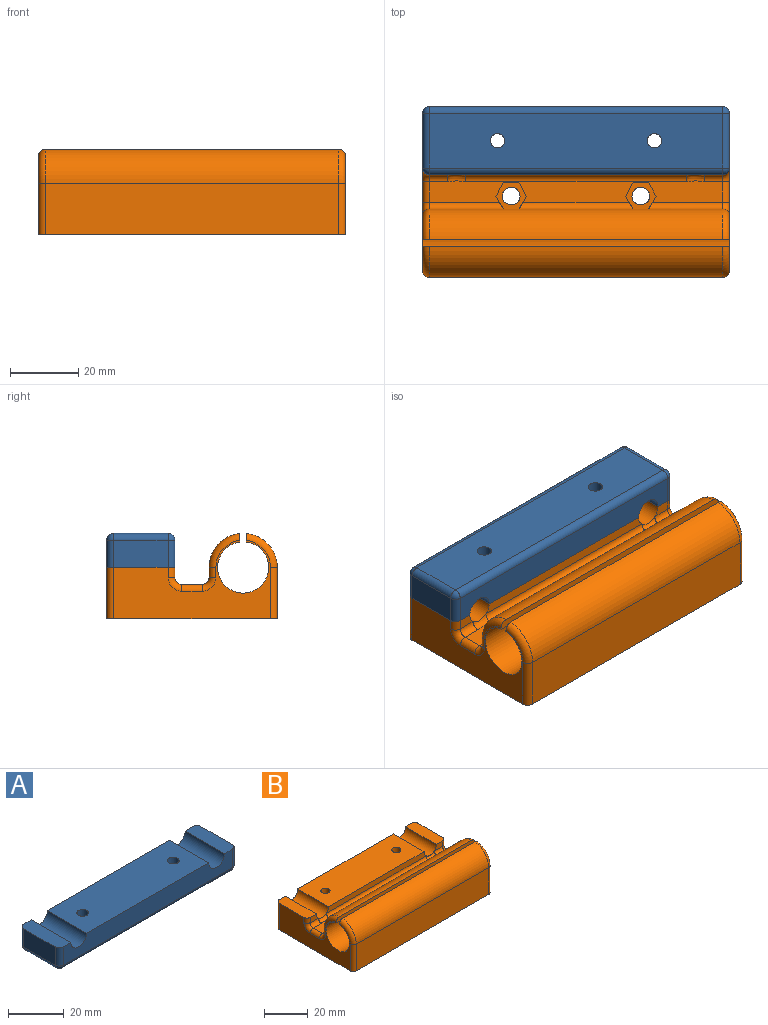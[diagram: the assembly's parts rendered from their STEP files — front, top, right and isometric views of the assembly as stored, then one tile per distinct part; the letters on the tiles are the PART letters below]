
ASSEMBLY  parts=2 mates=1
PART A: 24 faces, bbox 90x20x10 mm
  f0: plane 62x20mm, normal (0,0,1), area 1212.3mm2, adj f2,f4,f8,f9,f10,f11
  f1: plane 20x6mm, normal (0,0,1), area 118.3mm2, adj f2,f3,f4,f10,f14,f23
  f2: plane 86x8mm, normal (0,-1,0), area 637.7mm2, adj f0,f1,f6,f10,f11,f17,f21,f23
  f3: plane 16x8mm, normal (1,0,0), area 128mm2, adj f1,f14,f20,f23
  f4: plane 86x8mm, normal (0,1,0), area 637.7mm2, adj f0,f1,f6,f10,f11,f12,f14,f15
  f5: plane 16x8mm, normal (-1,0,0), area 128mm2, adj f6,f12,f16,f17
  f6: plane 20x6mm, normal (0,0,1), area 118.3mm2, adj f2,f4,f5,f11,f12,f17
  f7: plane 86x16mm, normal (0,0,-1), area 1348.3mm2, adj f8,f9,f15,f16,f20,f21
  f8: cylinder r=2.1mm len=10mm, axis (0,0,1), area 131.9mm2, adj f0,f7
  f9: cylinder r=2.1mm len=10mm, axis (0,0,1), area 131.9mm2, adj f0,f7
  f10: cylinder r=4mm len=20mm, axis (0,-1,0), area 251.3mm2, adj f0,f1,f2,f4
  f11: cylinder r=4mm len=20mm, axis (0,-1,0), area 251.3mm2, adj f0,f2,f4,f6
  f12: cylinder r=2mm len=8mm, axis (0,0,1), area 25.1mm2, adj f4,f5,f6,f13
  f13: sphere r=2mm, area 6.3mm2, adj f12,f15,f16
  f14: cylinder r=2mm len=8mm, axis (0,0,-1), area 25.1mm2, adj f1,f3,f4,f18
  f15: cylinder r=2mm len=86mm, axis (-1,0,0), area 270.2mm2, adj f4,f7,f13,f18
  f16: cylinder r=2mm len=16mm, axis (0,-1,0), area 50.3mm2, adj f5,f7,f13,f19
  f17: cylinder r=2mm len=8mm, axis (0,0,-1), area 25.1mm2, adj f2,f5,f6,f19
  f18: sphere r=2mm, area 6.3mm2, adj f14,f15,f20
  f19: sphere r=2mm, area 6.3mm2, adj f16,f17,f21
  f20: cylinder r=2mm len=16mm, axis (0,1,0), area 50.3mm2, adj f3,f7,f18,f22
  f21: cylinder r=2mm len=86mm, axis (1,0,0), area 270.2mm2, adj f2,f7,f19,f22
  f22: sphere r=2mm, area 6.3mm2, adj f20,f21,f23
  f23: cylinder r=2mm len=8mm, axis (0,0,1), area 25.1mm2, adj f1,f2,f3,f22
PART B: 271 faces, bbox 90.5x51.3x26.3 mm
  f0: plane 90x50mm, normal (0,0,-1), area 4154.4mm2, adj f7,f9,f10,f11,f13,f15,f36,f37
  f1: plane 5.35x3mm, normal (0,-1,0), area 13.2mm2, adj f6,f34,f55,f57
  f2: plane 64.71x3mm, normal (0,-1,0), area 188.5mm2, adj f5,f34,f35,f62
  f3: cylinder r=2.1mm len=11.5mm, axis (0,0,1), area 151.7mm2, adj f5,f49
  f4: cylinder r=2.1mm len=11.5mm, axis (0,0,1), area 151.7mm2, adj f5,f42
  f5: plane 62x20mm, normal (0,0,1), area 1212.3mm2, adj f2,f3,f4,f7,f34,f35
  f6: plane 20x6mm, normal (0,0,1), area 118.3mm2, adj f1,f7,f11,f34,f55,f75
  f7: plane 86x15mm, normal (0,1,0), area 1239.7mm2, adj f0,f5,f6,f33,f34,f35,f74,f75
  f8: plane 86x6.27mm, normal (0,0,1), area 436.2mm2, adj f20,f21,f22,f23,f24,f26,f27,f28
  f9: cylinder r=2.6mm len=6mm, axis (0,0,-1), area 98mm2, adj f0,f31
  f10: cylinder r=2.6mm len=6mm, axis (0,0,-1), area 98mm2, adj f0,f25
  f11: plane 46x22.94mm, normal (-1,0,0), area 521.7mm2, adj f0,f6,f17,f18,f19,f50,f52,f53
  f12: cylinder r=10mm len=86mm, axis (-1,0,0), area 1267.5mm2, adj f14,f18,f50,f58
  f13: plane 46x22.94mm, normal (1,0,0), area 521.7mm2, adj f0,f17,f18,f19,f33,f58,f60,f63
  f14: plane 86x9mm, normal (0,1,0), area 313.3mm2, adj f12,f21,f22,f25,f26,f30,f31,f51
  f15: plane 86x15mm, normal (0,-1,0), area 1290mm2, adj f0,f16,f69,f72
  f16: cylinder r=10mm len=86mm, axis (-1,0,0), area 1267.5mm2, adj f15,f19,f70,f73
  f17: cylinder r=7.5mm len=90mm, axis (-1,0,0), area 4066.5mm2, adj f11,f13,f18,f19
  f18: plane 90.12x2.63mm, normal (0,-1,0), area 224.7mm2, adj f11,f12,f13,f17,f50,f58
  f19: plane 90.12x2.63mm, normal (0,1,0), area 224.7mm2, adj f11,f13,f16,f17,f70,f73
  f20: plane 4x3.9mm, normal (0.87,-0.5,0), area 18mm2, adj f8,f21,f24,f25
  f21: plane 6.49x4.29mm, normal (0.87,0.5,0), area 18.5mm2, adj f8,f14,f20,f25,f71
  f22: plane 6.49x4.29mm, normal (-0.87,0.5,0), area 18.5mm2, adj f8,f14,f23,f25,f61
  f23: plane 4x3.9mm, normal (-0.87,-0.5,0), area 18mm2, adj f8,f22,f24,f25
  f24: plane 4.5x4mm, normal (0,-1,0), area 18mm2, adj f8,f20,f23,f25
  f25: plane 9x7.7mm, normal (0,0,1), area 30.9mm2, adj f10,f14,f20,f21,f22,f23,f24
  f26: plane 6.49x4.29mm, normal (-0.87,0.5,0), area 18.5mm2, adj f8,f14,f27,f31,f71
  f27: plane 4x3.9mm, normal (-0.87,-0.5,0), area 18mm2, adj f8,f26,f28,f31
  f28: plane 4.5x4mm, normal (0,-1,0), area 18mm2, adj f8,f27,f29,f31
  f29: plane 4x3.9mm, normal (0.87,-0.5,0), area 18mm2, adj f8,f28,f30,f31
  f30: plane 6.49x4.29mm, normal (0.87,0.5,0), area 18.5mm2, adj f8,f14,f29,f31,f51
  f31: plane 9x7.7mm, normal (0,0,1), area 30.9mm2, adj f9,f14,f26,f27,f28,f29,f30
  f32: plane 5.35x3mm, normal (0,-1,0), area 13.2mm2, adj f33,f35,f66,f68
  f33: plane 20x6mm, normal (0,0,1), area 118.3mm2, adj f7,f13,f32,f35,f68,f74
  f34: cylinder r=4mm len=20mm, axis (0,1,0), area 251.3mm2, adj f1,f2,f5,f6,f7,f59
  f35: cylinder r=4mm len=20mm, axis (0,1,0), area 251.3mm2, adj f2,f5,f7,f32,f33,f64
  f36: plane 3.5x3.46mm, normal (0.87,0.5,0), area 14mm2, adj f0,f37,f41,f42
  f37: plane 3.5x3.46mm, normal (0.87,-0.5,0), area 14mm2, adj f0,f36,f38,f42
  f38: plane 4x3.5mm, normal (0,-1,0), area 14mm2, adj f0,f37,f39,f42
  f39: plane 3.5x3.46mm, normal (-0.87,-0.5,0), area 14mm2, adj f0,f38,f40,f42
  f40: plane 3.5x3.46mm, normal (-0.87,0.5,0), area 14mm2, adj f0,f39,f41,f42
  f41: plane 4x3.5mm, normal (0,1,0), area 14mm2, adj f0,f36,f40,f42
  f42: plane 8x6.93mm, normal (0,0,-1), area 27.7mm2, adj f4,f36,f37,f38,f39,f40,f41
  f43: plane 4x3.5mm, normal (0,-1,0), area 14mm2, adj f0,f44,f48,f49
  f44: plane 3.5x3.46mm, normal (-0.87,-0.5,0), area 14mm2, adj f0,f43,f45,f49
  f45: plane 3.5x3.46mm, normal (-0.87,0.5,0), area 14mm2, adj f0,f44,f46,f49
  f46: plane 4x3.5mm, normal (0,1,0), area 14mm2, adj f0,f45,f47,f49
  f47: plane 3.5x3.46mm, normal (0.87,0.5,0), area 14mm2, adj f0,f46,f48,f49
  f48: plane 3.5x3.46mm, normal (0.87,-0.5,0), area 14mm2, adj f0,f43,f47,f49
  f49: plane 8x6.93mm, normal (0,0,-1), area 27.7mm2, adj f3,f43,f44,f45,f46,f47,f48
  f50: torus R=8mm, axis (-1,0,0), area 42.6mm2, adj f11,f12,f18,f52
  f51: cylinder r=2mm len=21.69mm, axis (-1,0,0), area 66.3mm2, adj f8,f14,f30,f53
  f52: cylinder r=2mm len=3mm, axis (0,0,1), area 9.4mm2, adj f11,f14,f50,f53
  f53: torus R=4mm, axis (-1,0,0), area 13.5mm2, adj f11,f51,f52,f54
  f54: cylinder r=2mm len=6mm, axis (0,1,0), area 18.8mm2, adj f8,f11,f53,f56
  f55: cylinder r=2mm len=3mm, axis (0,0,1), area 9.4mm2, adj f1,f6,f11,f56
  f56: torus R=4mm, axis (-1,0,0), area 13.5mm2, adj f11,f54,f55,f57
  f57: cylinder r=2mm len=5.35mm, axis (1,0,0), area 16.8mm2, adj f1,f8,f56,f59
  f58: torus R=8mm, axis (-1,0,0), area 42.6mm2, adj f12,f13,f18,f60
  f59: bspline ~5.29x2mm, area 13mm2, adj f8,f34,f57,f62
  f60: cylinder r=2mm len=3mm, axis (0,0,-1), area 9.4mm2, adj f13,f14,f58,f63
  f61: cylinder r=2mm len=21.69mm, axis (-1,0,0), area 66.3mm2, adj f8,f14,f22,f63
  f62: cylinder r=2mm len=64.71mm, axis (1,0,0), area 203.3mm2, adj f2,f8,f59,f64
  f63: torus R=4mm, axis (-1,0,0), area 13.5mm2, adj f13,f60,f61,f65
  f64: bspline ~5.29x2mm, area 13mm2, adj f8,f35,f62,f66
  f65: cylinder r=2mm len=6mm, axis (0,-1,0), area 18.8mm2, adj f8,f13,f63,f67
  f66: cylinder r=2mm len=5.35mm, axis (1,0,0), area 16.8mm2, adj f8,f32,f64,f67
  f67: torus R=4mm, axis (-1,0,0), area 13.5mm2, adj f13,f65,f66,f68
  f68: cylinder r=2mm len=3mm, axis (0,0,-1), area 9.4mm2, adj f13,f32,f33,f67
  f69: cylinder r=2mm len=15mm, axis (0,0,1), area 47.1mm2, adj f0,f13,f15,f70
  f70: torus R=8mm, axis (-1,0,0), area 42.6mm2, adj f13,f16,f19,f69
  f71: cylinder r=2mm len=33.39mm, axis (-1,0,0), area 101.3mm2, adj f8,f14,f21,f26
  f72: cylinder r=2mm len=15mm, axis (0,0,-1), area 47.1mm2, adj f0,f11,f15,f73
  f73: torus R=8mm, axis (-1,0,0), area 42.6mm2, adj f11,f16,f19,f72
  f74: cylinder r=2mm len=15mm, axis (0,0,-1), area 47.1mm2, adj f0,f7,f13,f33
  f75: cylinder r=2mm len=15mm, axis (0,0,1), area 47.1mm2, adj f0,f6,f7,f11
  f76: extruded ~1x0.5mm, area 0.6mm2, adj f0,f77,f269,f270
  f77: extruded ~1.04x1mm, area 1.3mm2, adj f0,f76,f78,f270
  f78: extruded ~1.1x1mm, area 1.5mm2, adj f0,f77,f79,f270
  f79: extruded ~1.93x1.26mm, area 2.3mm2, adj f0,f78,f80,f270
  f80: extruded ~2.5x1.47mm, area 2.9mm2, adj f0,f79,f81,f270
  f81: extruded ~1.02x1mm, area 1.1mm2, adj f0,f80,f82,f270
  f82: extruded ~1.07x1mm, area 1.2mm2, adj f0,f81,f83,f270
  f83: extruded ~1.71x1.61mm, area 2.4mm2, adj f0,f82,f84,f270
  f84: plane 1.38x1mm, normal (0.83,0.56,0), area 1.7mm2, adj f0,f83,f85,f270
  f85: plane 1.14x1mm, normal (-1,0.03,0), area 1.1mm2, adj f0,f84,f86,f270
  f86: extruded ~1.41x1mm, area 1.4mm2, adj f0,f85,f87,f270
  f87: extruded ~2.03x1mm, area 2.4mm2, adj f0,f86,f88,f270
  f88: plane 1x0.25mm, normal (0.78,0.63,0), area 0.3mm2, adj f0,f87,f89,f270
  f89: plane 7.66x1mm, normal (1,0,0), area 7.7mm2, adj f0,f88,f90,f270
  f90: plane 1x0.21mm, normal (0,1,0), area 0.2mm2, adj f0,f89,f91,f270
  f91: extruded ~1x0.29mm, area 0.3mm2, adj f0,f90,f92,f270
  f92: extruded ~1x0.82mm, area 0.8mm2, adj f0,f91,f93,f270
  f93: extruded ~1x0.87mm, area 0.9mm2, adj f0,f92,f94,f270
  f94: extruded ~1x0.4mm, area 0.5mm2, adj f0,f93,f95,f270
  f95: plane 1x0.23mm, normal (-0.8,-0.61,0), area 0.3mm2, adj f0,f94,f96,f270
  f96: plane 7.68x1mm, normal (-1,-0.01,0), area 7.7mm2, adj f0,f95,f97,f270
  f97: plane 1x0.15mm, normal (-0.14,-0.99,0), area 0.2mm2, adj f0,f96,f98,f270
  f98: extruded ~2.2x1mm, area 2.4mm2, adj f0,f97,f99,f270
  f99: extruded ~2.14x1mm, area 2.1mm2, adj f0,f98,f100,f270
  f100: extruded ~1x0.32mm, area 0.3mm2, adj f0,f99,f101,f270
  f101: plane 1x0.24mm, normal (0,-1,0), area 0.2mm2, adj f0,f100,f102,f270
  f102: plane 1.71x1.15mm, normal (-0.83,-0.56,0), area 2.1mm2, adj f0,f101,f103,f270
  f103: extruded ~2.7x2.03mm, area 3.4mm2, adj f0,f102,f104,f270
  f104: extruded ~2.32x1.28mm, area 2.8mm2, adj f0,f103,f105,f270
  f105: extruded ~2.24x1.37mm, area 2.6mm2, adj f0,f104,f106,f270
  f106: extruded ~1.05x1mm, area 1.1mm2, adj f0,f105,f107,f270
  f107: extruded ~2.15x1.86mm, area 2.9mm2, adj f0,f106,f108,f270
  f108: plane 1.17x1mm, normal (0.62,-0.79,0), area 1.5mm2, adj f0,f107,f109,f270
  f109: plane 4.11x1mm, normal (-0.01,-1,0), area 4.1mm2, adj f0,f108,f110,f270
  f110: plane 1x0.26mm, normal (-0.55,-0.83,0), area 0.3mm2, adj f0,f109,f111,f270
  f111: extruded ~1.07x1mm, area 1.2mm2, adj f0,f110,f112,f270
  f112: extruded ~1.06x1mm, area 1.5mm2, adj f0,f111,f113,f270
  f113: extruded ~3.15x1.9mm, area 3.9mm2, adj f0,f112,f114,f270
  f114: extruded ~2.12x1.03mm, area 2.4mm2, adj f0,f113,f115,f270
  f115: extruded ~3.61x1mm, area 3.9mm2, adj f0,f114,f116,f270
  f116: extruded ~1.4x1.35mm, area 2mm2, adj f0,f115,f117,f270
  f117: extruded ~3.77x1mm, area 4.1mm2, adj f0,f116,f118,f270
  f118: extruded ~1.03x1mm, area 1.3mm2, adj f0,f117,f119,f270
  f119: extruded ~1x0.75mm, area 1mm2, adj f0,f118,f120,f270
  f120: extruded ~1.34x1mm, area 1.4mm2, adj f0,f119,f121,f270
  f121: extruded ~3.83x1mm, area 3.9mm2, adj f0,f120,f122,f270
  f122: extruded ~3.45x1mm, area 3.4mm2, adj f0,f121,f123,f270
  f123: extruded ~1x0.74mm, area 1mm2, adj f0,f122,f124,f270
  f124: extruded ~1.02x1mm, area 1mm2, adj f0,f123,f125,f270
  f125: extruded ~1x0.85mm, area 1.1mm2, adj f0,f124,f126,f270
  f126: extruded ~2.26x1.79mm, area 3mm2, adj f0,f125,f127,f270
  f127: extruded ~2.86x1mm, area 3.1mm2, adj f0,f126,f128,f270
  f128: extruded ~4.57x1mm, area 5.1mm2, adj f0,f127,f129,f270
  f129: extruded ~2.52x1mm, area 2.8mm2, adj f0,f128,f130,f270
  f130: extruded ~2.7x1.86mm, area 3.4mm2, adj f0,f129,f131,f270
  f131: extruded ~1x0.7mm, area 0.9mm2, adj f0,f130,f132,f270
  f132: extruded ~1.68x1mm, area 2mm2, adj f0,f131,f133,f270
  f133: extruded ~2.29x1mm, area 2.3mm2, adj f0,f132,f134,f270
  f134: extruded ~2.17x1mm, area 2.2mm2, adj f0,f133,f135,f270
  f135: extruded ~1x0.31mm, area 0.4mm2, adj f0,f134,f136,f270
  f136: extruded ~3.96x1mm, area 4mm2, adj f0,f135,f137,f270
  f137: extruded ~3.86x1mm, area 3.9mm2, adj f0,f136,f138,f270
  f138: extruded ~3.16x1mm, area 3.2mm2, adj f0,f137,f139,f270
  f139: extruded ~1.27x1mm, area 1.7mm2, adj f0,f138,f140,f270
  f140: extruded ~1.82x1.73mm, area 2.9mm2, adj f0,f139,f141,f270
  f141: extruded ~1.37x1.13mm, area 2mm2, adj f0,f140,f142,f270
  f142: extruded ~1x0.58mm, area 0.6mm2, adj f0,f141,f143,f270
  f143: extruded ~1.83x1.74mm, area 2.5mm2, adj f0,f142,f144,f270
  f144: plane 1.65x1.65mm, normal (0.71,-0.71,0), area 2.3mm2, adj f0,f143,f145,f270
  f145: plane 1x0.74mm, normal (0,-1,0), area 0.7mm2, adj f0,f144,f146,f270
  f146: extruded ~1.4x1mm, area 1.6mm2, adj f0,f145,f147,f270
  f147: extruded ~4.06x1mm, area 4.1mm2, adj f0,f146,f148,f270
  f148: extruded ~3.86x1mm, area 3.9mm2, adj f0,f147,f149,f270
  f149: extruded ~3.94x2.05mm, area 4.4mm2, adj f0,f148,f150,f270
  f150: extruded ~4.42x2.75mm, area 5.3mm2, adj f0,f149,f151,f270
  f151: extruded ~1x0.6mm, area 0.6mm2, adj f0,f150,f152,f270
  f152: extruded ~1x0.44mm, area 0.6mm2, adj f0,f151,f153,f270
  f153: extruded ~4.06x1mm, area 4.1mm2, adj f0,f152,f154,f270
  f154: plane 3.88x1mm, normal (-1,0,0), area 3.9mm2, adj f0,f153,f155,f270
  f155: plane 2.81x1mm, normal (-0.01,-1,0), area 2.8mm2, adj f0,f154,f156,f270
  f156: extruded ~2.98x1mm, area 3mm2, adj f0,f155,f157,f270
  f157: extruded ~1x0.33mm, area 0.5mm2, adj f0,f156,f158,f270
  f158: extruded ~1.87x1mm, area 1.9mm2, adj f0,f157,f159,f270
  f159: extruded ~2.03x1mm, area 2mm2, adj f0,f158,f160,f270
  f160: extruded ~1.14x1mm, area 1.5mm2, adj f0,f159,f161,f270
  f161: extruded ~1x0.75mm, area 0.8mm2, adj f0,f160,f162,f270
  f162: extruded ~1.97x1mm, area 2.1mm2, adj f0,f161,f163,f270
  f163: plane 1.4x1mm, normal (0.02,-1,0), area 1.4mm2, adj f0,f162,f164,f270
  f164: plane 1x0.33mm, normal (1,0,0), area 0.3mm2, adj f0,f163,f165,f270
  f165: plane 1.4x1mm, normal (0.02,1,0), area 1.4mm2, adj f0,f164,f166,f270
  f166: extruded ~1.97x1mm, area 2.1mm2, adj f0,f165,f167,f270
  f167: extruded ~1.88x1mm, area 2.3mm2, adj f0,f166,f168,f270
  f168: extruded ~2x1mm, area 2mm2, adj f0,f167,f169,f270
  f169: extruded ~1.9x1mm, area 2.1mm2, adj f0,f168,f170,f270
  f170: extruded ~1.8x1mm, area 1.8mm2, adj f0,f169,f171,f270
  f171: extruded ~2.02x1mm, area 2mm2, adj f0,f170,f172,f270
  f172: extruded ~1.44x1mm, area 1.9mm2, adj f0,f171,f173,f270
  f173: extruded ~1x0.84mm, area 1.2mm2, adj f0,f172,f174,f270
  f174: extruded ~4.85x1mm, area 4.9mm2, adj f0,f173,f175,f270
  f175: plane 4.6x1mm, normal (0,-1,0), area 4.6mm2, adj f0,f174,f176,f270
  f176: plane 1x0.23mm, normal (-0.57,-0.82,0), area 0.3mm2, adj f0,f175,f177,f270
  f177: extruded ~1x0.39mm, area 0.5mm2, adj f0,f176,f178,f270
  f178: plane 1x0.23mm, normal (-0.82,-0.57,0), area 0.3mm2, adj f0,f177,f179,f270
  f179: plane 3.03x1mm, normal (-1,-0.01,0), area 3mm2, adj f0,f178,f180,f270
  f180: extruded ~3.73x1mm, area 3.8mm2, adj f0,f179,f181,f270
  f181: extruded ~1.74x1mm, area 1.9mm2, adj f0,f180,f182,f270
  f182: plane 1.24x1mm, normal (-0.03,1,0), area 1.2mm2, adj f0,f181,f183,f270
  f183: plane 1x0.33mm, normal (-1,0,0), area 0.3mm2, adj f0,f182,f184,f270
  f184: plane 1x0.88mm, normal (-0.05,-1,0), area 0.9mm2, adj f0,f183,f185,f270
  f185: extruded ~6.03x1mm, area 6mm2, adj f0,f184,f186,f270
  f186: extruded ~1x0.2mm, area 0.3mm2, adj f0,f185,f187,f270
  f187: extruded ~1.26x1mm, area 1.3mm2, adj f0,f186,f188,f270
  f188: extruded ~1.44x1mm, area 1.5mm2, adj f0,f187,f189,f270
  f189: extruded ~1x0.69mm, area 0.9mm2, adj f0,f188,f190,f270
  f190: extruded ~6.33x1mm, area 6.3mm2, adj f0,f189,f191,f270
  f191: extruded ~1x0.71mm, area 1mm2, adj f0,f190,f192,f270
  f192: extruded ~2.33x1mm, area 2.3mm2, adj f0,f191,f193,f270
  f193: plane 2.06x1mm, normal (0,-1,0), area 2.1mm2, adj f0,f192,f194,f270
  f194: plane 1x0.97mm, normal (-1,0,0), area 1mm2, adj f0,f193,f195,f270
  f195: plane 4.03x1mm, normal (0,1,0), area 4mm2, adj f0,f194,f196,f270
  f196: plane 1x0.17mm, normal (-0.93,0.36,0), area 0.2mm2, adj f0,f195,f197,f270
  f197: extruded ~5.71x1mm, area 5.7mm2, adj f0,f196,f198,f270
  f198: plane 1x0.17mm, normal (-0.93,-0.36,0), area 0.2mm2, adj f0,f197,f199,f270
  f199: plane 1.16x1mm, normal (0,-1,0), area 1.2mm2, adj f0,f198,f200,f270
  f200: extruded ~1.42x1mm, area 1.4mm2, adj f0,f199,f201,f270
  f201: extruded ~1.8x1mm, area 2.1mm2, adj f0,f200,f202,f270
  f202: extruded ~4.24x1mm, area 4.4mm2, adj f0,f201,f203,f270
  f203: extruded ~4.21x1mm, area 4.3mm2, adj f0,f202,f204,f270
  f204: extruded ~1.31x1mm, area 1.4mm2, adj f0,f203,f205,f270
  f205: extruded ~1.94x1mm, area 2.2mm2, adj f0,f204,f206,f270
  f206: extruded ~1.17x1mm, area 1.2mm2, adj f0,f205,f207,f270
  f207: extruded ~5.89x1mm, area 5.9mm2, adj f0,f206,f208,f270
  f208: extruded ~4.51x1mm, area 4.5mm2, adj f0,f207,f209,f270
  f209: extruded ~4.57x1mm, area 4.7mm2, adj f0,f208,f210,f270
  f210: extruded ~2.44x1mm, area 2.5mm2, adj f0,f209,f211,f270
  f211: extruded ~1.94x1mm, area 2mm2, adj f0,f210,f212,f270
  f212: extruded ~1.9x1mm, area 2.3mm2, adj f0,f211,f213,f270
  f213: extruded ~2.01x1mm, area 2mm2, adj f0,f212,f214,f270
  f214: extruded ~2.08x1mm, area 2.1mm2, adj f0,f213,f215,f270
  f215: extruded ~1.36x1mm, area 1.5mm2, adj f0,f214,f216,f270
  f216: extruded ~1.46x1mm, area 1.5mm2, adj f0,f215,f217,f270
  f217: extruded ~1x0.77mm, area 1.1mm2, adj f0,f216,f218,f270
  f218: extruded ~1.28x1mm, area 1.4mm2, adj f0,f217,f219,f270
  f219: extruded ~1.94x1mm, area 2.1mm2, adj f0,f218,f220,f270
  f220: extruded ~1.41x1mm, area 1.4mm2, adj f0,f219,f221,f270
  f221: extruded ~2.06x1mm, area 2.2mm2, adj f0,f220,f222,f270
  f222: plane 1.93x1mm, normal (-0.01,-1,0), area 1.9mm2, adj f0,f221,f223,f270
  f223: plane 1x0.24mm, normal (-0.56,-0.83,0), area 0.3mm2, adj f0,f222,f224,f270
  f224: extruded ~1.13x1mm, area 1.3mm2, adj f0,f223,f225,f270
  f225: extruded ~1.1x1.04mm, area 1.6mm2, adj f0,f224,f226,f270
  f226: extruded ~3.27x1mm, area 3.3mm2, adj f0,f225,f227,f270
  f227: extruded ~3.11x1mm, area 3.1mm2, adj f0,f226,f228,f270
  f228: extruded ~1x0.31mm, area 0.4mm2, adj f0,f227,f229,f270
  f229: extruded ~4.08x1mm, area 4.1mm2, adj f0,f228,f230,f270
  f230: extruded ~3.87x1mm, area 3.9mm2, adj f0,f229,f231,f270
  f231: extruded ~3.95x2.05mm, area 4.5mm2, adj f0,f230,f232,f270
  f232: extruded ~4.08x2.07mm, area 4.6mm2, adj f0,f231,f233,f270
  f233: extruded ~1x0.97mm, area 1.1mm2, adj f0,f232,f234,f270
  f234: extruded ~1x0.84mm, area 1.1mm2, adj f0,f233,f235,f270
  f235: extruded ~3.98x1mm, area 4mm2, adj f0,f234,f236,f270
  f236: plane 3.77x1mm, normal (1,0,0), area 3.8mm2, adj f0,f235,f237,f270
  f237: plane 1x0.94mm, normal (0,1,0), area 0.9mm2, adj f0,f236,f238,f270
  f238: plane 1.45x1.45mm, normal (-0.71,0.71,0), area 2.1mm2, adj f0,f237,f239,f270
  f239: extruded ~1.81x1.43mm, area 2.9mm2, adj f0,f238,f240,f270
  f240: extruded ~2.4x1.61mm, area 3.1mm2, adj f0,f239,f241,f270
  f241: extruded ~2.17x1mm, area 2.2mm2, adj f0,f240,f242,f270
  f242: extruded ~1x1mm, area 1.4mm2, adj f0,f241,f243,f270
  f243: extruded ~2.44x1mm, area 2.5mm2, adj f0,f242,f244,f270
  f244: extruded ~1.84x1mm, area 1.9mm2, adj f0,f243,f245,f270
  f245: extruded ~1x0.68mm, area 1mm2, adj f0,f244,f246,f270
  f246: extruded ~3.91x1mm, area 3.9mm2, adj f0,f245,f247,f270
  f247: plane 3.67x1mm, normal (1,0,0), area 3.7mm2, adj f0,f246,f248,f270
  f248: plane 1.74x1mm, normal (0,1,0), area 1.7mm2, adj f0,f247,f249,f270
  f249: extruded ~1.9x1mm, area 2mm2, adj f0,f248,f250,f270
  f250: extruded ~1x0.44mm, area 0.5mm2, adj f0,f249,f251,f270
  f251: extruded ~1.44x1.14mm, area 1.9mm2, adj f0,f250,f252,f270
  f252: extruded ~5.55x1.22mm, area 6.1mm2, adj f0,f251,f253,f270
  f253: extruded ~3.84x1.24mm, area 4.2mm2, adj f0,f252,f254,f270
  f254: extruded ~6.23x3.31mm, area 8mm2, adj f0,f253,f255,f270
  f255: extruded ~1.69x1.58mm, area 2.3mm2, adj f0,f254,f256,f270
  f256: extruded ~1x0.51mm, area 0.8mm2, adj f0,f255,f257,f270
  f257: extruded ~3.15x1mm, area 3.1mm2, adj f0,f256,f258,f270
  f258: extruded ~3.15x1mm, area 3.1mm2, adj f0,f257,f259,f270
  f259: extruded ~1x0.16mm, area 0.2mm2, adj f0,f258,f260,f270
  f260: extruded ~1x0.5mm, area 0.6mm2, adj f0,f259,f261,f270
  f261: extruded ~1.84x1.83mm, area 2.6mm2, adj f0,f260,f262,f270
  f262: extruded ~3.77x1mm, area 3.9mm2, adj f0,f261,f263,f270
  f263: extruded ~1.84x1.84mm, area 2.6mm2, adj f0,f262,f264,f270
  f264: extruded ~6.09x4.4mm, area 8.8mm2, adj f0,f263,f265,f270
  f265: extruded ~3.46x2.27mm, area 4.3mm2, adj f0,f264,f266,f270
  f266: extruded ~1x0.56mm, area 0.7mm2, adj f0,f265,f267,f270
  f267: extruded ~1.87x1mm, area 2mm2, adj f0,f266,f268,f270
  f268: plane 1.71x1mm, normal (0,1,0), area 1.7mm2, adj f0,f267,f269,f270
  f269: plane 1x0.39mm, normal (-0.61,0.79,0), area 0.5mm2, adj f0,f76,f268,f270
  f270: plane 58.3x9.84mm, normal (0,0,-1), area 216.5mm2, adj f76,f77,f78,f79,f80,f81,f82,f83
PLACE A rot(axis=(-1,0,0),180deg) t=(-22.78,75.96,57.05)mm
PLACE B t=(-22.78,60.96,32.05)mm
MATE fastened B.f5 <-> A.f0  axis (0,0,1) through (-22.78,75.96,47.05)mm
